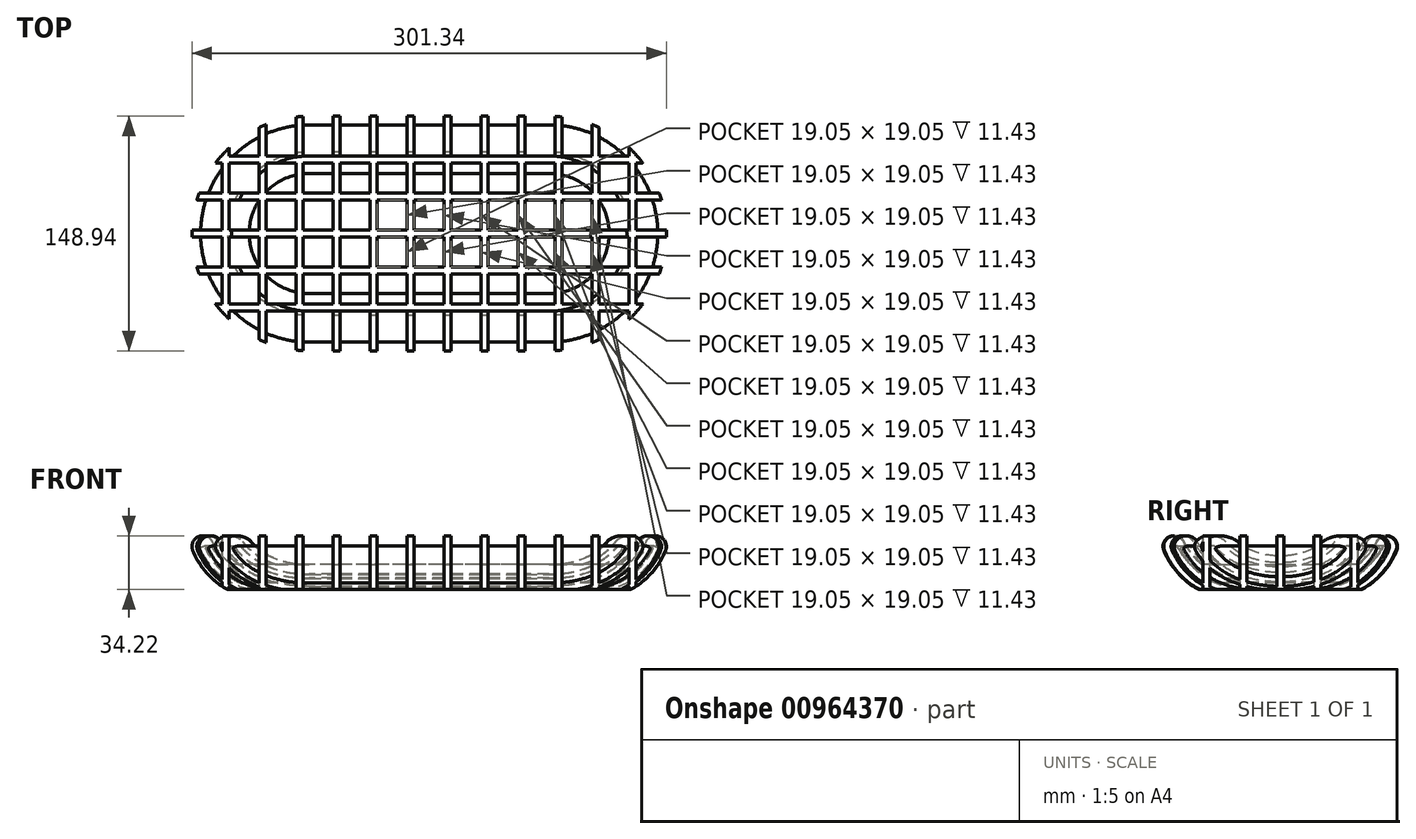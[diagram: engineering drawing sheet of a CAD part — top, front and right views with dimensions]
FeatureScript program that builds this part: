
annotation { "Feature Type Name" : "Feature", "Feature Type Description" : "" }
export const myFeature = defineFeature(function(context is Context, id is Id, definition is map)
    precondition{}
    {
        {
            var Q0;
            Q0=qCreatedBy(makeId("Top.planeOp"),FACE);
            var sketch = newSketch(context, id + "F0", { "sketchPlane" : qUnion([Q0])});
            skArc(sketch, "E0", {"start": v(-76.2, 38.1) * mm, "mid": v(-114.3, 0) * mm, "end": v(-76.2, -38.1) * mm});
            skArc(sketch, "E1", {"start": v(76.2, -38.1) * mm, "mid": v(114.3, 0) * mm, "end": v(76.2, 38.1) * mm});
            skLineSegment(sketch, "E2", {"start": v(-76.2, 38.1) * mm, "end": v(76.2, 38.1) * mm});
            skLineSegment(sketch, "E3", {"start": v(-76.2, -38.1) * mm, "end": v(76.2, -38.1) * mm});
            skLineSegment(sketch, "E4", {"start": v(-76.2, 0) * mm, "end": v(0, 0) * mm, "construction": true});
            skLineSegment(sketch, "E5", {"start": v(76.2, 0) * mm, "end": v(0, 0) * mm, "construction": true});
            skSolve(sketch);
        }
        {
            var Q0;
            Q0 = qSketchRegion(id + "F0", true);
            extrude(context, id + "F1", {"entities" : qUnion([Q0]), "depth" : 4.44 * mm, "offsetDistance" : 25.4 * mm});
        }
        {
            var Q0;
            Q0=qCreatedBy(makeId("Right.planeOp"),FACE);
            var Q1;
            Q1=sQuery(id+"F0.wireOp",VERTEX,"E0.end");
            cPlane(context, id + "F2", {"entities" : qUnion([Q0, Q1]), "cplaneType" : CPlaneType.PLANE_POINT, "offset" : 25.4 * mm, "width" : 152.4 * mm, "height" : 152.4 * mm});
        }
        {
            var Q0;
            Q0=qCreatedBy(id+"F2.planeOp",FACE);
            var sketch = newSketch(context, id + "F3", { "sketchPlane" : qUnion([Q0])});
            skArc(sketch, "E6", {"start": v(-69.38, 26.7) * mm, "mid": v(-56.98, 9.56) * mm, "end": v(-38.1, 0) * mm});
            skArc(sketch, "E7", {"start": v(-65.92, 28.11) * mm, "mid": v(-54.33, 13.55) * mm, "end": v(-38.1, 4.44) * mm});
            skLineSegment(sketch, "E8", {"start": v(-65.92, 28.11) * mm, "end": v(-69.38, 26.7) * mm});
            skLineSegment(sketch, "E9", {"start": v(-38.1, 4.45) * mm, "end": v(-38.1, 0) * mm});
            skSolve(sketch);
        }
        {
            var Q0;
            Q0=makeQuery(id+"F3.imprint","IMPRINT",FACE,{"disambiguationData":[TD([[makeQuery(id+"F3.imprint","IMPRINT",EDGE,{"derivedFrom":sQuery(id+"F3.wireOp",EDGE,"E6")}),1.0]])]});
            var Q1;
            Q1=sQuery(id+"F0.wireOp",EDGE,"E0");
            var Q2;
            Q2=sQuery(id+"F0.wireOp",EDGE,"E2");
            var Q3;
            Q3=sQuery(id+"F0.wireOp",EDGE,"E1");
            var Q4;
            Q4=sQuery(id+"F0.wireOp",EDGE,"E3");
            sweep(context, id + "F4", {"profiles" : qUnion([Q0]), "path" : qUnion([Q1, Q2, Q3, Q4])});
        }
        {
            var Q0;
            Q0=qCreatedBy(makeId("Top.planeOp"),FACE);
            cPlane(context, id + "F5", {"entities" : qUnion([Q0]), "cplaneType" : CPlaneType.OFFSET, "offset" : 50.8 * mm, "width" : 152.4 * mm, "height" : 152.4 * mm});
        }
        {
            var Q0;
            Q0=qCreatedBy(id+"F5.planeOp",FACE);
            var sketch = newSketch(context, id + "F6", { "sketchPlane" : qUnion([Q0])});
            skLineSegment(sketch, "E10.bottom", {"start": v(-131.44, 120.18) * mm, "end": v(-127, 120.18) * mm});
            skLineSegment(sketch, "E10.top", {"start": v(-131.44, -120.18) * mm, "end": v(-127, -120.18) * mm});
            skLineSegment(sketch, "E10.left", {"start": v(-131.44, 120.18) * mm, "end": v(-131.44, -120.18) * mm});
            skLineSegment(sketch, "E10.right", {"start": v(-127, 120.18) * mm, "end": v(-127, -120.18) * mm});
            skLineSegment(sketch, "E11.bottom", {"start": v(-107.95, 120.18) * mm, "end": v(-103.5, 120.18) * mm});
            skLineSegment(sketch, "E11.top", {"start": v(-107.95, -120.18) * mm, "end": v(-103.5, -120.18) * mm});
            skLineSegment(sketch, "E11.left", {"start": v(-107.95, 120.18) * mm, "end": v(-107.95, -120.18) * mm});
            skLineSegment(sketch, "E11.right", {"start": v(-103.5, 120.18) * mm, "end": v(-103.5, -120.18) * mm});
            skLineSegment(sketch, "E12.bottom", {"start": v(-84.45, 120.18) * mm, "end": v(-80, 120.18) * mm});
            skLineSegment(sketch, "E12.top", {"start": v(-84.45, -120.18) * mm, "end": v(-80, -120.18) * mm});
            skLineSegment(sketch, "E12.left", {"start": v(-84.45, 120.18) * mm, "end": v(-84.45, -120.18) * mm});
            skLineSegment(sketch, "E12.right", {"start": v(-80, 120.18) * mm, "end": v(-80, -120.18) * mm});
            skLineSegment(sketch, "E13.bottom", {"start": v(-60.96, 120.18) * mm, "end": v(-56.51, 120.18) * mm});
            skLineSegment(sketch, "E13.top", {"start": v(-60.96, -120.18) * mm, "end": v(-56.51, -120.18) * mm});
            skLineSegment(sketch, "E13.left", {"start": v(-60.96, 120.18) * mm, "end": v(-60.96, -120.18) * mm});
            skLineSegment(sketch, "E13.right", {"start": v(-56.51, 120.18) * mm, "end": v(-56.51, -120.18) * mm});
            skLineSegment(sketch, "E14.bottom", {"start": v(-37.46, 120.18) * mm, "end": v(-33.02, 120.18) * mm});
            skLineSegment(sketch, "E14.top", {"start": v(-37.46, -120.18) * mm, "end": v(-33.02, -120.18) * mm});
            skLineSegment(sketch, "E14.left", {"start": v(-37.46, 120.18) * mm, "end": v(-37.46, -120.18) * mm});
            skLineSegment(sketch, "E14.right", {"start": v(-33.02, 120.18) * mm, "end": v(-33.02, -120.18) * mm});
            skLineSegment(sketch, "E15", {"start": v(-127, 120.18) * mm, "end": v(-107.95, 120.18) * mm, "construction": true});
            skLineSegment(sketch, "E16", {"start": v(-103.5, 120.18) * mm, "end": v(-84.45, 120.18) * mm, "construction": true});
            skLineSegment(sketch, "E17", {"start": v(-56.51, 120.18) * mm, "end": v(-37.46, 120.18) * mm, "construction": true});
            skLineSegment(sketch, "E18", {"start": v(-80, 120.18) * mm, "end": v(-60.96, 120.18) * mm, "construction": true});
            skLineSegment(sketch, "E19", {"start": v(0, 0) * mm, "end": v(-131.44, 0) * mm, "construction": true});
            skLineSegment(sketch, "E20", {"start": v(-33.02, 120.18) * mm, "end": v(-13.97, 120.18) * mm, "construction": true});
            skLineSegment(sketch, "E21.bottom", {"start": v(-13.97, 120.18) * mm, "end": v(-9.52, 120.18) * mm});
            skLineSegment(sketch, "E21.top", {"start": v(-13.97, -120.18) * mm, "end": v(-9.52, -120.18) * mm});
            skLineSegment(sketch, "E21.left", {"start": v(-13.97, 120.18) * mm, "end": v(-13.97, -120.18) * mm});
            skLineSegment(sketch, "E21.right", {"start": v(-9.52, 120.18) * mm, "end": v(-9.53, -120.18) * mm});
            skLineSegment(sketch, "E22.bottom", {"start": v(9.53, 120.18) * mm, "end": v(13.97, 120.18) * mm});
            skLineSegment(sketch, "E22.top", {"start": v(9.53, -120.18) * mm, "end": v(13.97, -120.18) * mm});
            skLineSegment(sketch, "E22.left", {"start": v(9.53, 120.18) * mm, "end": v(9.53, -120.18) * mm});
            skLineSegment(sketch, "E22.right", {"start": v(13.97, 120.18) * mm, "end": v(13.97, -120.18) * mm});
            skLineSegment(sketch, "E23.bottom", {"start": v(33.02, 120.18) * mm, "end": v(37.47, 120.18) * mm});
            skLineSegment(sketch, "E23.top", {"start": v(33.02, -120.18) * mm, "end": v(37.47, -120.18) * mm});
            skLineSegment(sketch, "E23.left", {"start": v(33.02, 120.18) * mm, "end": v(33.02, -120.18) * mm});
            skLineSegment(sketch, "E23.right", {"start": v(37.47, 120.18) * mm, "end": v(37.47, -120.18) * mm});
            skLineSegment(sketch, "E24.bottom", {"start": v(56.52, 120.18) * mm, "end": v(60.96, 120.18) * mm});
            skLineSegment(sketch, "E24.top", {"start": v(56.52, -120.18) * mm, "end": v(60.96, -120.18) * mm});
            skLineSegment(sketch, "E24.left", {"start": v(56.52, 120.18) * mm, "end": v(56.52, -120.18) * mm});
            skLineSegment(sketch, "E24.right", {"start": v(60.96, 120.18) * mm, "end": v(60.96, -120.18) * mm});
            skLineSegment(sketch, "E25.bottom", {"start": v(80.01, 120.18) * mm, "end": v(84.45, 120.18) * mm});
            skLineSegment(sketch, "E25.top", {"start": v(80.01, -120.18) * mm, "end": v(84.46, -120.18) * mm});
            skLineSegment(sketch, "E25.left", {"start": v(80.01, 120.18) * mm, "end": v(80.01, -120.18) * mm});
            skLineSegment(sketch, "E25.right", {"start": v(84.46, 120.18) * mm, "end": v(84.46, -120.18) * mm});
            skLineSegment(sketch, "E26.bottom", {"start": v(103.5, 120.18) * mm, "end": v(107.95, 120.18) * mm});
            skLineSegment(sketch, "E26.top", {"start": v(103.5, -120.18) * mm, "end": v(107.95, -120.18) * mm});
            skLineSegment(sketch, "E26.left", {"start": v(103.5, 120.18) * mm, "end": v(103.5, -120.18) * mm});
            skLineSegment(sketch, "E26.right", {"start": v(107.95, 120.18) * mm, "end": v(107.95, -120.18) * mm});
            skLineSegment(sketch, "E27", {"start": v(84.45, 120.18) * mm, "end": v(103.5, 120.18) * mm, "construction": true});
            skLineSegment(sketch, "E28", {"start": v(60.96, 120.18) * mm, "end": v(80.01, 120.18) * mm, "construction": true});
            skLineSegment(sketch, "E29", {"start": v(37.47, 120.18) * mm, "end": v(56.52, 120.18) * mm, "construction": true});
            skLineSegment(sketch, "E30", {"start": v(13.97, 120.18) * mm, "end": v(33.02, 120.18) * mm, "construction": true});
            skLineSegment(sketch, "E31", {"start": v(-9.52, 120.18) * mm, "end": v(9.53, 120.18) * mm, "construction": true});
            skLineSegment(sketch, "E32", {"start": v(-9.53, 0) * mm, "end": v(0, 69.38) * mm, "construction": true});
            skLineSegment(sketch, "E33", {"start": v(0, 69.38) * mm, "end": v(9.53, 0) * mm, "construction": true});
            skLineSegment(sketch, "E34.bottom", {"start": v(127, 120.18) * mm, "end": v(131.44, 120.18) * mm});
            skLineSegment(sketch, "E34.top", {"start": v(127, -120.18) * mm, "end": v(131.45, -120.18) * mm});
            skLineSegment(sketch, "E34.left", {"start": v(127, 120.18) * mm, "end": v(127, -120.18) * mm});
            skLineSegment(sketch, "E34.right", {"start": v(131.44, 120.18) * mm, "end": v(131.44, -120.18) * mm});
            skLineSegment(sketch, "E35", {"start": v(107.95, 120.18) * mm, "end": v(127, 120.18) * mm});
            skSolve(sketch);
        }
        {
            var Q0;
            Q0 = qSketchRegion(id + "F6", true);
            extrude(context, id + "F7", {"entities" : qUnion([Q0]), "oppositeDirection" : true, "depth" : 63.5 * mm, "offsetDistance" : 25.4 * mm});
        }
        {
            var Q0;
            Q0=qCreatedBy(id+"F5.planeOp",FACE);
            var sketch = newSketch(context, id + "F8", { "sketchPlane" : qUnion([Q0])});
            skLineSegment(sketch, "E36.bottom", {"start": v(-183.68, 2.35) * mm, "end": v(183.68, 2.35) * mm});
            skLineSegment(sketch, "E36.top", {"start": v(-183.68, -2.1) * mm, "end": v(183.68, -2.1) * mm});
            skLineSegment(sketch, "E36.left", {"start": v(-183.68, 2.35) * mm, "end": v(-183.68, -2.1) * mm});
            skLineSegment(sketch, "E36.right", {"start": v(183.68, 2.35) * mm, "end": v(183.68, -2.1) * mm});
            skLineSegment(sketch, "E37.bottom", {"start": v(-183.68, 25.84) * mm, "end": v(183.68, 25.84) * mm});
            skLineSegment(sketch, "E37.top", {"start": v(-183.68, 21.4) * mm, "end": v(183.68, 21.4) * mm});
            skLineSegment(sketch, "E37.left", {"start": v(-183.68, 25.84) * mm, "end": v(-183.68, 21.4) * mm});
            skLineSegment(sketch, "E37.right", {"start": v(183.68, 25.84) * mm, "end": v(183.68, 21.4) * mm});
            skLineSegment(sketch, "E38.bottom", {"start": v(-183.68, 49.34) * mm, "end": v(183.68, 49.34) * mm});
            skLineSegment(sketch, "E38.top", {"start": v(-183.68, 44.9) * mm, "end": v(183.68, 44.9) * mm});
            skLineSegment(sketch, "E38.left", {"start": v(-183.68, 49.34) * mm, "end": v(-183.68, 44.9) * mm});
            skLineSegment(sketch, "E38.right", {"start": v(183.68, 49.34) * mm, "end": v(183.68, 44.9) * mm});
            skLineSegment(sketch, "E39.bottom", {"start": v(-183.68, -21.15) * mm, "end": v(183.68, -21.15) * mm});
            skLineSegment(sketch, "E39.top", {"start": v(-183.68, -25.6) * mm, "end": v(183.68, -25.6) * mm});
            skLineSegment(sketch, "E39.left", {"start": v(-183.68, -21.15) * mm, "end": v(-183.68, -25.6) * mm});
            skLineSegment(sketch, "E39.right", {"start": v(183.68, -21.15) * mm, "end": v(183.68, -25.6) * mm});
            skLineSegment(sketch, "E40.bottom", {"start": v(-183.68, -44.64) * mm, "end": v(183.68, -44.64) * mm});
            skLineSegment(sketch, "E40.top", {"start": v(-183.68, -49.09) * mm, "end": v(183.68, -49.09) * mm});
            skLineSegment(sketch, "E40.left", {"start": v(-183.68, -44.64) * mm, "end": v(-183.68, -49.09) * mm});
            skLineSegment(sketch, "E40.right", {"start": v(183.68, -44.64) * mm, "end": v(183.68, -49.09) * mm});
            skLineSegment(sketch, "E41", {"start": v(183.68, 44.9) * mm, "end": v(183.68, 25.84) * mm, "construction": true});
            skLineSegment(sketch, "E42", {"start": v(183.68, 21.4) * mm, "end": v(183.68, 2.35) * mm, "construction": true});
            skLineSegment(sketch, "E43", {"start": v(183.68, -2.1) * mm, "end": v(183.68, -21.15) * mm, "construction": true});
            skLineSegment(sketch, "E44", {"start": v(183.68, -25.6) * mm, "end": v(183.68, -44.64) * mm, "construction": true});
            skLineSegment(sketch, "E45", {"start": v(0, 0) * mm, "end": v(0, 2.35) * mm, "construction": true});
            skLineSegment(sketch, "E46", {"start": v(0, 0) * mm, "end": v(183.68, 0) * mm, "construction": true});
            skSolve(sketch);
        }
        {
            var Q0;
            Q0 = qSketchRegion(id + "F8", true);
            extrude(context, id + "F9", {"entities" : qUnion([Q0]), "oppositeDirection" : true, "depth" : 63.5 * mm, "offsetDistance" : 25.4 * mm});
        }
        {
            var Q0;
            Q0=makeQuery(id+"F4.opSweep","SWEPT_EDGE",EDGE,{"disambiguationData":[OSD([sQuery(id+"F0.wireOp",EDGE,"E0"),sQuery(id+"F3.wireOp",EDGE,"E6"),sQuery(id+"F3.wireOp",EDGE,"E8")])]});
            fillet(context, id + "F10", {"entities" : qUnion([Q0]), "radius" : 1.27 * mm, "tangentPropagation" : true, "allowEdgeOverflow" : false});
        }
        {
            var Q0;
            Q0=makeQuery(id+"F4.opSweep","SWEPT_EDGE",EDGE,{"disambiguationData":[OSD([sQuery(id+"F0.wireOp",EDGE,"E0"),sQuery(id+"F3.wireOp",EDGE,"E7"),sQuery(id+"F3.wireOp",EDGE,"E8")])]});
            fillet(context, id + "F11", {"entities" : qUnion([Q0]), "radius" : 1.27 * mm, "tangentPropagation" : true, "allowEdgeOverflow" : false});
        }
        {
            var Q0;
            Q0=makeQuery(id+"F4.opSweep","SWEPT_BODY",BODY,{"disambiguationData":[OSD([sQuery(id+"F0.wireOp",EDGE,"E2"),sQuery(id+"F3.wireOp",EDGE,"E6"),sQuery(id+"F3.wireOp",EDGE,"E7"),sQuery(id+"F3.wireOp",EDGE,"E8"),sQuery(id+"F3.wireOp",EDGE,"E9")])]});
            var Q1;
            Q1=makeQuery(id+"F7.opExtrude","SWEPT_BODY",BODY,{"disambiguationData":[OSD([sQuery(id+"F6.wireOp",EDGE,"E10.bottom"),sQuery(id+"F6.wireOp",EDGE,"E10.top"),sQuery(id+"F6.wireOp",EDGE,"E10.left"),sQuery(id+"F6.wireOp",EDGE,"E10.right")])]});
            var Q2;
            Q2=makeQuery(id+"F7.opExtrude","SWEPT_BODY",BODY,{"disambiguationData":[OSD([sQuery(id+"F6.wireOp",EDGE,"E11.bottom"),sQuery(id+"F6.wireOp",EDGE,"E11.top"),sQuery(id+"F6.wireOp",EDGE,"E11.left"),sQuery(id+"F6.wireOp",EDGE,"E11.right")])]});
            var Q3;
            Q3=makeQuery(id+"F7.opExtrude","SWEPT_BODY",BODY,{"disambiguationData":[OSD([sQuery(id+"F6.wireOp",EDGE,"E12.bottom"),sQuery(id+"F6.wireOp",EDGE,"E12.top"),sQuery(id+"F6.wireOp",EDGE,"E12.left"),sQuery(id+"F6.wireOp",EDGE,"E12.right")])]});
            var Q4;
            Q4=makeQuery(id+"F7.opExtrude","SWEPT_BODY",BODY,{"disambiguationData":[OSD([sQuery(id+"F6.wireOp",EDGE,"E13.bottom"),sQuery(id+"F6.wireOp",EDGE,"E13.top"),sQuery(id+"F6.wireOp",EDGE,"E13.left"),sQuery(id+"F6.wireOp",EDGE,"E13.right")])]});
            var Q5;
            Q5=makeQuery(id+"F7.opExtrude","SWEPT_BODY",BODY,{"disambiguationData":[OSD([sQuery(id+"F6.wireOp",EDGE,"E14.bottom"),sQuery(id+"F6.wireOp",EDGE,"E14.top"),sQuery(id+"F6.wireOp",EDGE,"E14.left"),sQuery(id+"F6.wireOp",EDGE,"E14.right")])]});
            var Q6;
            Q6=makeQuery(id+"F7.opExtrude","SWEPT_BODY",BODY,{"disambiguationData":[OSD([sQuery(id+"F6.wireOp",EDGE,"E21.bottom"),sQuery(id+"F6.wireOp",EDGE,"E21.top"),sQuery(id+"F6.wireOp",EDGE,"E21.left"),sQuery(id+"F6.wireOp",EDGE,"E21.right")])]});
            var Q7;
            Q7=makeQuery(id+"F7.opExtrude","SWEPT_BODY",BODY,{"disambiguationData":[OSD([sQuery(id+"F6.wireOp",EDGE,"E22.bottom"),sQuery(id+"F6.wireOp",EDGE,"E22.top"),sQuery(id+"F6.wireOp",EDGE,"E22.left"),sQuery(id+"F6.wireOp",EDGE,"E22.right")])]});
            var Q8;
            Q8=makeQuery(id+"F7.opExtrude","SWEPT_BODY",BODY,{"disambiguationData":[OSD([sQuery(id+"F6.wireOp",EDGE,"E23.bottom"),sQuery(id+"F6.wireOp",EDGE,"E23.top"),sQuery(id+"F6.wireOp",EDGE,"E23.left"),sQuery(id+"F6.wireOp",EDGE,"E23.right")])]});
            var Q9;
            Q9=makeQuery(id+"F7.opExtrude","SWEPT_BODY",BODY,{"disambiguationData":[OSD([sQuery(id+"F6.wireOp",EDGE,"E24.bottom"),sQuery(id+"F6.wireOp",EDGE,"E24.top"),sQuery(id+"F6.wireOp",EDGE,"E24.left"),sQuery(id+"F6.wireOp",EDGE,"E24.right")])]});
            var Q10;
            Q10=makeQuery(id+"F7.opExtrude","SWEPT_BODY",BODY,{"disambiguationData":[OSD([sQuery(id+"F6.wireOp",EDGE,"E25.bottom"),sQuery(id+"F6.wireOp",EDGE,"E25.top"),sQuery(id+"F6.wireOp",EDGE,"E25.left"),sQuery(id+"F6.wireOp",EDGE,"E25.right")])]});
            var Q11;
            Q11=makeQuery(id+"F7.opExtrude","SWEPT_BODY",BODY,{"disambiguationData":[OSD([sQuery(id+"F6.wireOp",EDGE,"E26.bottom"),sQuery(id+"F6.wireOp",EDGE,"E26.top"),sQuery(id+"F6.wireOp",EDGE,"E26.left"),sQuery(id+"F6.wireOp",EDGE,"E26.right")])]});
            var Q12;
            Q12=makeQuery(id+"F7.opExtrude","SWEPT_BODY",BODY,{"disambiguationData":[OSD([sQuery(id+"F6.wireOp",EDGE,"E34.bottom"),sQuery(id+"F6.wireOp",EDGE,"E34.top"),sQuery(id+"F6.wireOp",EDGE,"E34.left"),sQuery(id+"F6.wireOp",EDGE,"E34.right")])]});
            var Q13;
            Q13=makeQuery(id+"F9.opExtrude","SWEPT_BODY",BODY,{"disambiguationData":[OSD([sQuery(id+"F8.wireOp",EDGE,"E36.bottom"),sQuery(id+"F8.wireOp",EDGE,"E36.top"),sQuery(id+"F8.wireOp",EDGE,"E36.left"),sQuery(id+"F8.wireOp",EDGE,"E36.right")])]});
            var Q14;
            Q14=makeQuery(id+"F9.opExtrude","SWEPT_BODY",BODY,{"disambiguationData":[OSD([sQuery(id+"F8.wireOp",EDGE,"E37.bottom"),sQuery(id+"F8.wireOp",EDGE,"E37.top"),sQuery(id+"F8.wireOp",EDGE,"E37.left"),sQuery(id+"F8.wireOp",EDGE,"E37.right")])]});
            var Q15;
            Q15=makeQuery(id+"F9.opExtrude","SWEPT_BODY",BODY,{"disambiguationData":[OSD([sQuery(id+"F8.wireOp",EDGE,"E38.bottom"),sQuery(id+"F8.wireOp",EDGE,"E38.top"),sQuery(id+"F8.wireOp",EDGE,"E38.left"),sQuery(id+"F8.wireOp",EDGE,"E38.right")])]});
            var Q16;
            Q16=makeQuery(id+"F9.opExtrude","SWEPT_BODY",BODY,{"disambiguationData":[OSD([sQuery(id+"F8.wireOp",EDGE,"E39.bottom"),sQuery(id+"F8.wireOp",EDGE,"E39.top"),sQuery(id+"F8.wireOp",EDGE,"E39.left"),sQuery(id+"F8.wireOp",EDGE,"E39.right")])]});
            var Q17;
            Q17=makeQuery(id+"F9.opExtrude","SWEPT_BODY",BODY,{"disambiguationData":[OSD([sQuery(id+"F8.wireOp",EDGE,"E40.bottom"),sQuery(id+"F8.wireOp",EDGE,"E40.top"),sQuery(id+"F8.wireOp",EDGE,"E40.left"),sQuery(id+"F8.wireOp",EDGE,"E40.right")])]});
            var Q18;
            Q18=makeQuery(id+"F1.opExtrude","SWEPT_BODY",BODY,{"disambiguationData":[OSD([sQuery(id+"F0.wireOp",EDGE,"E0"),sQuery(id+"F0.wireOp",EDGE,"E1"),sQuery(id+"F0.wireOp",EDGE,"E2"),sQuery(id+"F0.wireOp",EDGE,"E3")])]});
            booleanBodies(context, id + "F12", {"operationType" : BooleanOperationType.UNION, "tools" : qUnion([Q0, Q1, Q2, Q3, Q4, Q5, Q6, Q7, Q8, Q9, Q10, Q11, Q12, Q13, Q14, Q15, Q16, Q17, Q18])});
        }
        {
            var Q0;
            Q0=qCreatedBy(id+"F2.planeOp",FACE);
            var sketch = newSketch(context, id + "F13", { "sketchPlane" : qUnion([Q0])});
            skArc(sketch, "E47", {"start": v(-61.6, 30.53) * mm, "mid": v(-70.5, 33.6) * mm, "end": v(-73.96, 24.82) * mm});
            skArc(sketch, "E48", {"start": v(-73.96, 24.82) * mm, "mid": v(-64.07, 9.48) * mm, "end": v(-49.31, -1.27) * mm});
            skLineSegment(sketch, "E49", {"start": v(-49.31, -1.27) * mm, "end": v(0, -1.27) * mm});
            skLineSegment(sketch, "E50", {"start": v(0, -1.27) * mm, "end": v(0, 0) * mm});
            skLineSegment(sketch, "E51", {"start": v(0, 0) * mm, "end": v(0, 15.88) * mm});
            skLineSegment(sketch, "E52", {"start": v(0, 15.88) * mm, "end": v(-49.31, 15.87) * mm});
            skArc(sketch, "E53", {"start": v(-61.6, 30.53) * mm, "mid": v(-56.27, 22.52) * mm, "end": v(-49.31, 15.88) * mm});
            skLineSegment(sketch, "E54", {"start": v(0, 15.88) * mm, "end": v(0, 76.2) * mm});
            skLineSegment(sketch, "E55", {"start": v(0, -1.27) * mm, "end": v(0, -38.1) * mm});
            skLineSegment(sketch, "E56", {"start": v(0, -38.1) * mm, "end": v(-145.58, -38.1) * mm});
            skLineSegment(sketch, "E57", {"start": v(-145.58, -38.1) * mm, "end": v(-145.58, 76.2) * mm});
            skLineSegment(sketch, "E58", {"start": v(-145.58, 76.2) * mm, "end": v(0, 76.2) * mm});
            skSolve(sketch);
        }
        {
            var Q0;
            Q0=qCreatedBy(id+"F2.planeOp",FACE);
            var sketch = newSketch(context, id + "F14", { "sketchPlane" : qUnion([Q0])});
            skArc(sketch, "E59.0", {"start": v(-61.6, 30.53) * mm, "mid": v(-56.27, 22.52) * mm, "end": v(-49.31, 15.88) * mm});
            skArc(sketch, "E59.1", {"start": v(-73.96, 24.82) * mm, "mid": v(-64.07, 9.48) * mm, "end": v(-49.31, -1.27) * mm});
            skArc(sketch, "E60.0", {"start": v(-61.6, 30.53) * mm, "mid": v(-70.5, 33.6) * mm, "end": v(-73.96, 24.82) * mm});
            skLineSegment(sketch, "E61", {"start": v(-49.31, 15.88) * mm, "end": v(-49.31, 76.2) * mm});
            skLineSegment(sketch, "E62", {"start": v(-49.31, 76.2) * mm, "end": v(-145.58, 76.2) * mm});
            skLineSegment(sketch, "E63", {"start": v(-145.58, 76.2) * mm, "end": v(-145.58, -38.1) * mm});
            skLineSegment(sketch, "E64", {"start": v(-145.58, -38.1) * mm, "end": v(-49.31, -38.1) * mm});
            skLineSegment(sketch, "E65", {"start": v(-49.31, -38.1) * mm, "end": v(-49.31, -1.27) * mm});
            skSolve(sketch);
        }
        {
            var Q0;
            Q0=makeQuery(id+"F14.imprint","IMPRINT",FACE,{"disambiguationData":[TD([[makeQuery(id+"F14.imprint","IMPRINT",EDGE,{"derivedFrom":sQuery(id+"F14.wireOp",EDGE,"E59.0")}),1.0]])]});
            var Q1;
            Q1=sQuery(id+"F0.wireOp",EDGE,"E0");
            var Q2;
            Q2=sQuery(id+"F0.wireOp",EDGE,"E2");
            var Q3;
            Q3=sQuery(id+"F0.wireOp",EDGE,"E1");
            var Q4;
            Q4=sQuery(id+"F0.wireOp",EDGE,"E3");
            sweep(context, id + "F15", {"operationType" : NewBodyOperationType.REMOVE, "profiles" : qUnion([Q0]), "path" : qUnion([Q1, Q2, Q3, Q4])});
        }
        {
            var Q0;
            Q0=qCreatedBy(makeId("Top.planeOp"),FACE);
            var Q1;
            Q1=sQuery(id+"F13.wireOp",VERTEX,"E52.end");
            cPlane(context, id + "F16", {"entities" : qUnion([Q0, Q1]), "cplaneType" : CPlaneType.PLANE_POINT, "offset" : 25.4 * mm, "width" : 152.4 * mm, "height" : 152.4 * mm});
        }
        {
            var Q0;
            Q0=qCreatedBy(makeId("Top.planeOp"),FACE);
            var Q1;
            Q1=sQuery(id+"F13.wireOp",VERTEX,"E48.end");
            cPlane(context, id + "F17", {"entities" : qUnion([Q0, Q1]), "cplaneType" : CPlaneType.PLANE_POINT, "offset" : 25.4 * mm, "width" : 152.4 * mm, "height" : 152.4 * mm});
        }
        {
            var Q0;
            Q0=qCreatedBy(id+"F16.planeOp",FACE);
            var sketch = newSketch(context, id + "F18", { "sketchPlane" : qUnion([Q0])});
            skArc(sketch, "E66", {"start": v(-76.2, 49.31) * mm, "mid": v(-125.51, 0) * mm, "end": v(-76.2, -49.31) * mm});
            skArc(sketch, "E67", {"start": v(76.2, -49.31) * mm, "mid": v(125.51, 0) * mm, "end": v(76.2, 49.31) * mm});
            skLineSegment(sketch, "E68", {"start": v(-76.2, 49.31) * mm, "end": v(76.2, 49.31) * mm});
            skLineSegment(sketch, "E69", {"start": v(-76.2, -49.31) * mm, "end": v(76.2, -49.31) * mm});
            skLineSegment(sketch, "E70", {"start": v(-76.2, 0) * mm, "end": v(0, 0) * mm, "construction": true});
            skLineSegment(sketch, "E71", {"start": v(0, 0) * mm, "end": v(76.2, 0) * mm, "construction": true});
            skSolve(sketch);
        }
        {
            var Q0;
            Q0=qCreatedBy(id+"F17.planeOp",FACE);
            var sketch = newSketch(context, id + "F19", { "sketchPlane" : qUnion([Q0])});
            skArc(sketch, "E72", {"start": v(-76.2, 49.31) * mm, "mid": v(-125.51, 0) * mm, "end": v(-76.2, -49.31) * mm});
            skArc(sketch, "E73", {"start": v(76.2, -49.31) * mm, "mid": v(125.51, 0) * mm, "end": v(76.2, 49.31) * mm});
            skLineSegment(sketch, "E74", {"start": v(-76.2, 49.31) * mm, "end": v(76.2, 49.31) * mm});
            skLineSegment(sketch, "E75", {"start": v(76.2, -49.31) * mm, "end": v(-76.2, -49.31) * mm});
            skLineSegment(sketch, "E76", {"start": v(-76.2, 0) * mm, "end": v(0, 0) * mm, "construction": true});
            skLineSegment(sketch, "E77", {"start": v(0, 0) * mm, "end": v(76.2, 0) * mm, "construction": true});
            skSolve(sketch);
        }
        {
            var Q0;
            Q0 = qSketchRegion(id + "F18", true);
            extrude(context, id + "F20", {"entities" : qUnion([Q0]), "operationType" : NewBodyOperationType.REMOVE, "endBound" : BoundingType.THROUGH_ALL, "depth" : 25.4 * mm, "offsetDistance" : 25.4 * mm});
        }
        {
            var Q0;
            Q0 = qSketchRegion(id + "F19", true);
            extrude(context, id + "F21", {"entities" : qUnion([Q0]), "operationType" : NewBodyOperationType.REMOVE, "endBound" : BoundingType.THROUGH_ALL, "oppositeDirection" : true, "depth" : 25.4 * mm, "offsetDistance" : 25.4 * mm});
        }
        {
            var Q0;
            Q0=makeQuery(id+"F12.opBoolean","SPLIT",FACE,{"disambiguationData":[TD([makeQuery(id+"F7.opExtrude","SWEPT_FACE",FACE,{"disambiguationData":[OSD([sQuery(id+"F6.wireOp",EDGE,"E21.right")])]}),makeQuery(id+"F7.opExtrude","SWEPT_FACE",FACE,{"disambiguationData":[OSD([sQuery(id+"F6.wireOp",EDGE,"E22.left")])]}),makeQuery(id+"F9.opExtrude","SWEPT_FACE",FACE,{"disambiguationData":[OSD([sQuery(id+"F8.wireOp",EDGE,"E36.top")])]}),makeQuery(id+"F9.opExtrude","SWEPT_FACE",FACE,{"disambiguationData":[OSD([sQuery(id+"F8.wireOp",EDGE,"E39.bottom")])]})])],"derivedFrom":makeQuery(id+"F1.opExtrude","CAP_FACE",FACE,{"disambiguationData":[OSD([sQuery(id+"F0.wireOp",EDGE,"E0"),sQuery(id+"F0.wireOp",EDGE,"E1"),sQuery(id+"F0.wireOp",EDGE,"E2"),sQuery(id+"F0.wireOp",EDGE,"E3")])],"isStart":true})});
            var sketch = newSketch(context, id + "F22", { "sketchPlane" : qUnion([Q0])});
            skLineSegment(sketch, "E78.bottom", {"start": v(-186.73, 109.48) * mm, "end": v(188.77, 109.48) * mm});
            skLineSegment(sketch, "E78.top", {"start": v(-186.73, -123.25) * mm, "end": v(188.77, -123.25) * mm});
            skLineSegment(sketch, "E78.left", {"start": v(-186.73, 109.48) * mm, "end": v(-186.73, -123.25) * mm});
            skLineSegment(sketch, "E78.right", {"start": v(188.77, 109.48) * mm, "end": v(188.77, -123.25) * mm});
            skSolve(sketch);
        }
        {
            var Q0;
            Q0 = qSketchRegion(id + "F22", true);
            extrude(context, id + "F23", {"entities" : qUnion([Q0]), "operationType" : NewBodyOperationType.REMOVE, "endBound" : BoundingType.THROUGH_ALL, "depth" : 25.4 * mm, "offsetDistance" : 25.4 * mm});
        }
    });
